# Revit family: SNS Merlin 2000X Gas Pressure Proving
name_source: partatom
category: Electrical Equipment
units: mm (PartAtom-declared; Revit-internal decimal feet)

## family parameters
Always vertical = Yes
Cut with Voids When Loaded = No
OmniClass Number = 23.80.30.11.17
OmniClass Title = Distribution Boards and Control Panels
Part Type = Other Panel
Room Calculation Point = No
Round Connector Dimension = Use Diameter
Shared = No
Work Plane-Based = No

## types (1)
- SNS Merlin 2000X
    Default Height = 4' - 0"
    Description = The Merlin 2000X is the ultimate gas pressure proving & ventilation interlock system, specifically designed for use in commercial kitchens to meet BS6173. This panel is designed for use when the kitchen appliances do not have flame failure devices fitted, therefore gas proving is a requirement.

The Merlin 2000X system uses two unique built in current monitors which displays the exact fan current, in order to interlock with the ventilation with precision accuracy. The system is compatible with both current monitors and air pressure differential switches in order to interlock with up to 4 fans.
    Load = 120 VA
    Manufacturer = S&S Northern Ltd.
    Model = SNS Merlin 2000X
    Product Information = https://snsnorthern.com
    Type Comments = The Merlin 2000X is the ultimate gas pressure proving & ventilation interlock system, specifically designed for use in commercial kitchens to meet BS6173. This panel is designed for use when the kitchen appliances do not have flame failure devices fitted, therefore gas proving is a requirement.

The Merlin 2000X system uses two unique built in current monitors which displays the exact fan current, in order to interlock with the ventilation with precision accuracy. The system is compatible with both current monitors and air pressure differential switches in order to interlock with up to 4 fans.
    URL = https://snsnorthern.com
    Voltage = 120VAC

## geometry (parser evidence)
native form markers: Sweep x11
no freeform markers — native parametric forms only
